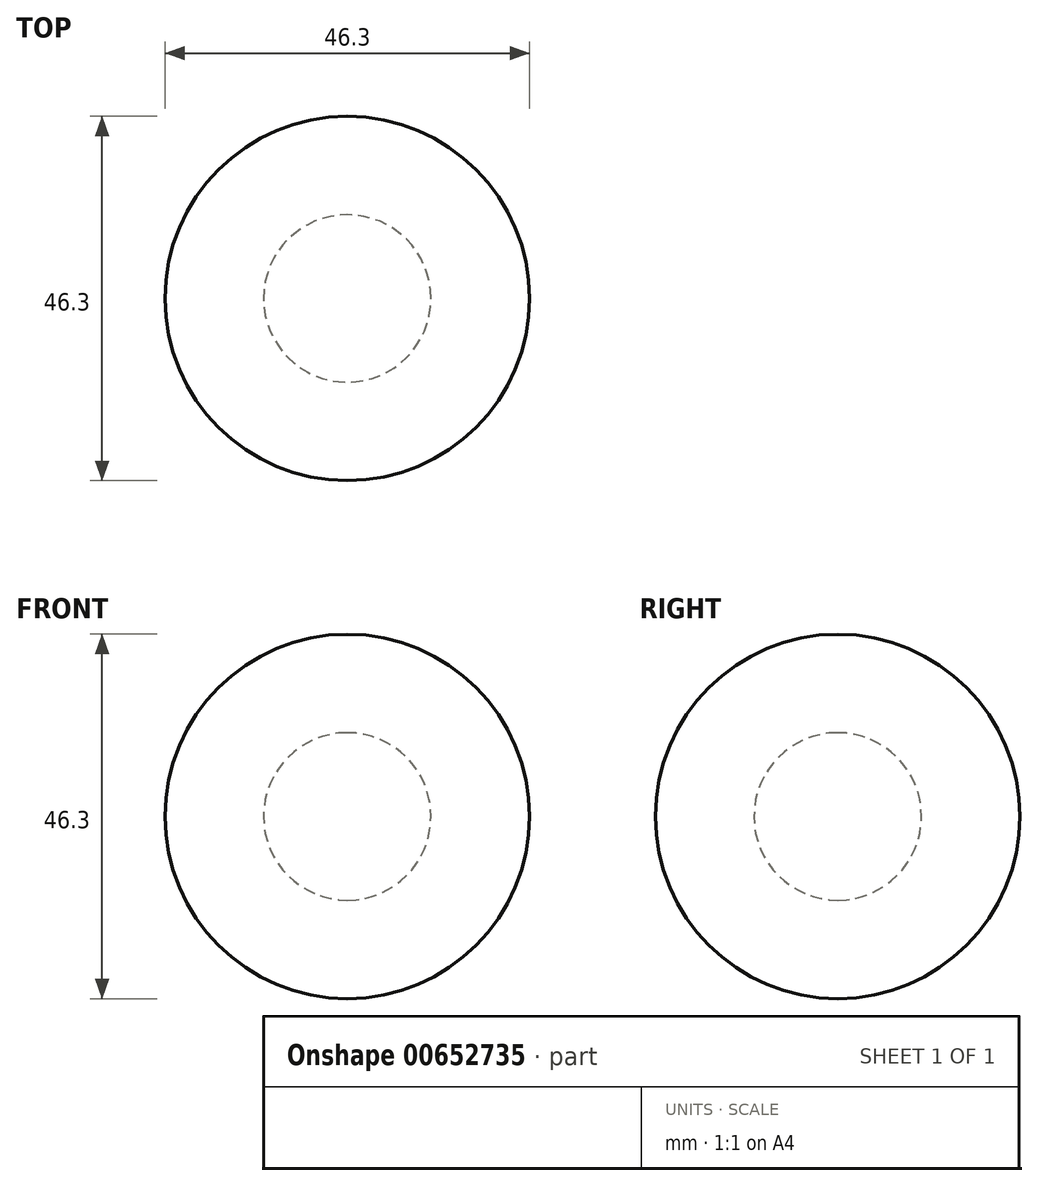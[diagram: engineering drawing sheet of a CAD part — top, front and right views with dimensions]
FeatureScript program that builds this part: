
annotation { "Feature Type Name" : "Feature", "Feature Type Description" : "" }
export const myFeature = defineFeature(function(context is Context, id is Id, definition is map)
    precondition{}
    {
        {
            var Q0;
            Q0=qCreatedBy(makeId("Front.planeOp"),FACE);
            var sketch = newSketch(context, id + "F0", { "sketchPlane" : qUnion([Q0])});
            skCircle(sketch, "E0", {"center": v(0, 0) * mm, "radius": 10.63 * mm});
            skCircle(sketch, "E1", {"center": v(0, 0) * mm, "radius": 23.15 * mm});
            skLineSegment(sketch, "E2", {"start": v(0, 44.08) * mm, "end": v(0, -44.77) * mm});
            skSolve(sketch);
        }
        {
            var Q0;
            {var subQ0=sQuery(id+"F0.wireOp",EDGE,"E2");var subQ1=sQuery(id+"F0.wireOp",EDGE,"E0");var subQ2=makeQuery(id+"F0.imprint","INTERSECT",VERTEX,{"disambiguationData":[OD(0.0)],"derivedFrom":[subQ1,subQ0]});Q0=makeQuery(id+"F0.imprint","IMPRINT",FACE,{"disambiguationData":[TD([[makeQuery(id+"F0.imprint","IMPRINT",EDGE,{"disambiguationData":[TD([[subQ2,-1.0]])],"derivedFrom":subQ1}),-1.0]])]});}
            var Q1;
            Q1=sQuery(id+"F0.wireOp",EDGE,"E2");
            revolve(context, id + "F1", {"entities" : qUnion([Q0]), "axis" : qUnion([Q1]), "revolveType" : RevolveType.FULL});
        }
    });
